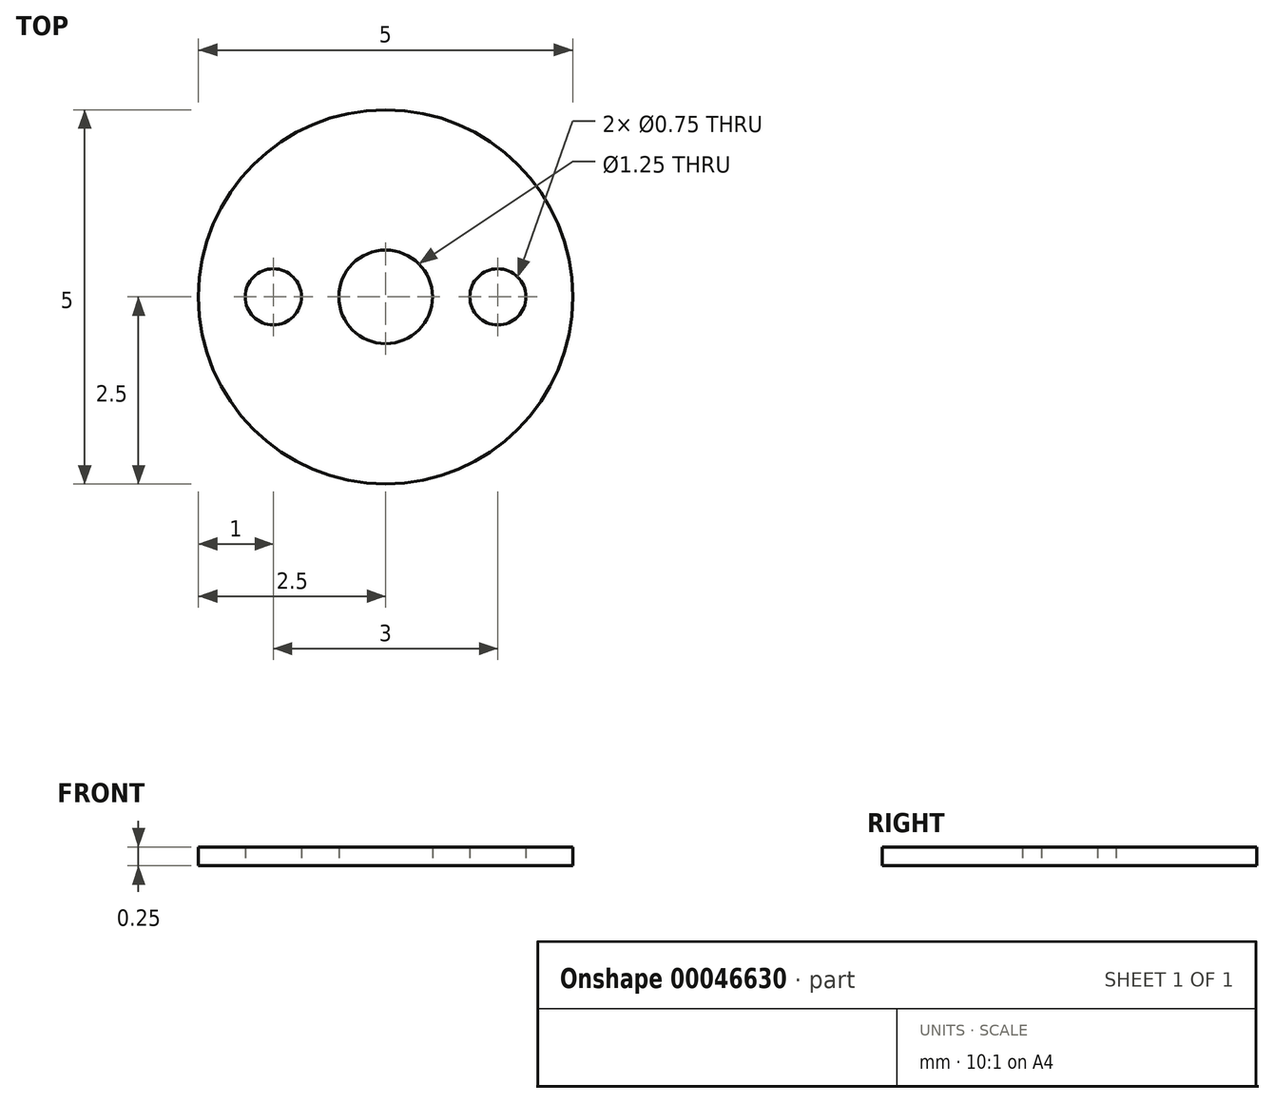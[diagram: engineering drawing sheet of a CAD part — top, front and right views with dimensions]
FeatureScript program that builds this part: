
annotation { "Feature Type Name" : "Feature", "Feature Type Description" : "" }
export const myFeature = defineFeature(function(context is Context, id is Id, definition is map)
    precondition{}
    {
        {
            var Q0;
            Q0=qCreatedBy(makeId("Top.planeOp"),FACE);
            var sketch = newSketch(context, id + "F0", { "sketchPlane" : qUnion([Q0])});
            skCircle(sketch, "E0", {"center": v(0, 0) * mm, "radius": 2.5 * mm});
            skCircle(sketch, "E1", {"center": v(0, 0) * mm, "radius": 0.62 * mm});
            skCircle(sketch, "E2", {"center": v(1.5, 0) * mm, "radius": 0.38 * mm});
            skCircle(sketch, "E3", {"center": v(-1.5, 0) * mm, "radius": 0.38 * mm});
            skSolve(sketch);
        }
        {
            var Q0;
            Q0=makeQuery(id+"F0.imprint","IMPRINT",FACE,{"disambiguationData":[TD([[makeQuery(id+"F0.imprint","IMPRINT",EDGE,{"derivedFrom":sQuery(id+"F0.wireOp",EDGE,"E0")}),1.0]])]});
            extrude(context, id + "F1", {"entities" : qUnion([Q0]), "depth" : 0.25 * mm});
        }
    });
